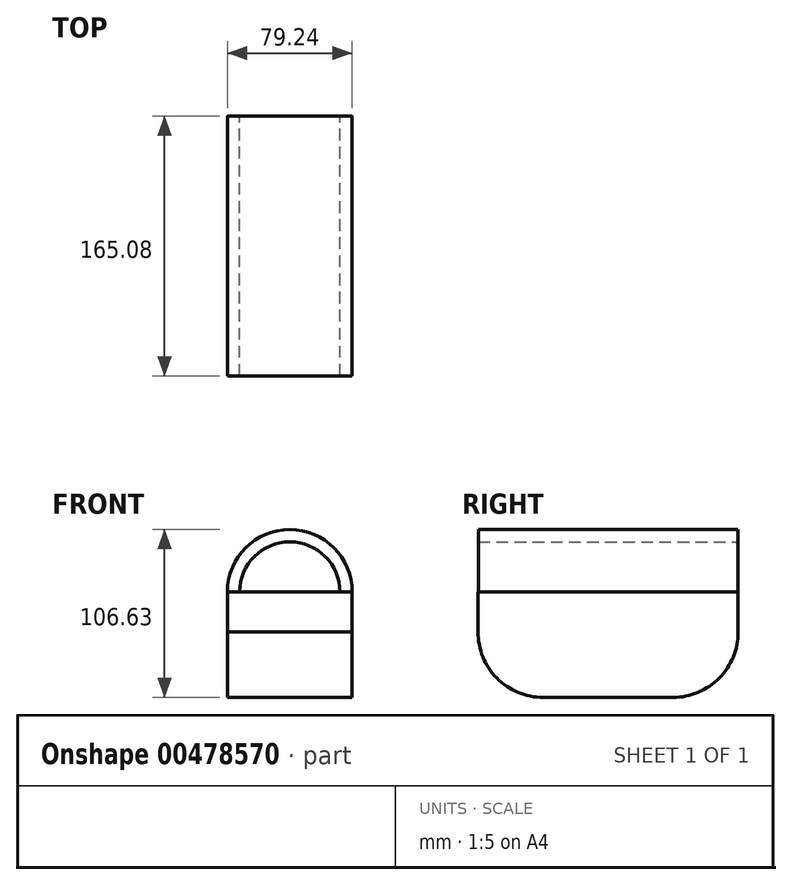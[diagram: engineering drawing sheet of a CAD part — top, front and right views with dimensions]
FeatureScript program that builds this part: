
annotation { "Feature Type Name" : "Feature", "Feature Type Description" : "" }
export const myFeature = defineFeature(function(context is Context, id is Id, definition is map)
    precondition{}
    {
        {
            var Q0;
            Q0=qCreatedBy(makeId("Front.planeOp"),FACE);
            var sketch = newSketch(context, id + "F0", { "sketchPlane" : qUnion([Q0])});
            skPoint(sketch, "E0.end.orphan", {"position": v(-39.32, 0) * mm});
            skPoint(sketch, "E0.start.orphan", {"position": v(39.32, 0) * mm});
            skArc(sketch, "E1", {"start": v(39.62, 0) * mm, "mid": v(0, 39.62) * mm, "end": v(-39.62, 0) * mm});
            skArc(sketch, "E2", {"start": v(31.8, 0) * mm, "mid": v(0, 31.8) * mm, "end": v(-31.8, 0) * mm});
            skLineSegment(sketch, "E3", {"start": v(39.32, 0) * mm, "end": v(39.62, 0) * mm});
            skLineSegment(sketch, "E4", {"start": v(31.8, 0) * mm, "end": v(39.62, 0) * mm});
            skPoint(sketch, "E5.end.orphan", {"position": v(-31.8, -66.6) * mm});
            skPoint(sketch, "E5.start.orphan", {"position": v(-39.62, -66.6) * mm});
            skLineSegment(sketch, "E6", {"start": v(-39.32, 0) * mm, "end": v(-31.8, 0) * mm});
            skLineSegment(sketch, "E7.MirrorCS", {"start": v(-31.8, 0) * mm, "end": v(-39.62, 0) * mm});
            skPoint(sketch, "E8.MirrorCS.start.orphan", {"position": v(-31.8, 0) * mm});
            skPoint(sketch, "E9.MirrorCS.start.orphan", {"position": v(-39.62, 0) * mm});
            skPoint(sketch, "E10.MirrorCS.end.orphan", {"position": v(31.8, -66.6) * mm});
            skPoint(sketch, "E10.MirrorCS.start.orphan", {"position": v(31.8, 0) * mm});
            skPoint(sketch, "E11.MirrorCS.end.orphan", {"position": v(39.62, -66.6) * mm});
            skPoint(sketch, "E11.MirrorCS.start.orphan", {"position": v(39.62, 0) * mm});
            skSolve(sketch);
        }
        {
            var Q0;
            {var subQ1=sQuery(id+"F0.wireOp",EDGE,"E1");Q0=makeQuery(id+"F0.imprint","IMPRINT",FACE,{"disambiguationData":[TD([[makeQuery(id+"F0.imprint","IMPRINT",EDGE,{"derivedFrom":subQ1}),1.0]])]});}
            extrude(context, id + "F1", {"entities" : qUnion([Q0]), "depth" : 82.42 * mm, "hasSecondDirection" : true, "secondDirectionOppositeDirection" : true, "secondDirectionDepth" : 82.42 * mm});
        }
        {
            var Q0;
            Q0=qCreatedBy(makeId("Right.planeOp"),FACE);
            var sketch = newSketch(context, id + "F2", { "sketchPlane" : qUnion([Q0])});
            skLineSegment(sketch, "E12", {"start": v(0, -67.01) * mm, "end": v(-41.35, -67.01) * mm});
            skLineSegment(sketch, "E13", {"start": v(-82.53, 0) * mm, "end": v(-82.53, -25.34) * mm});
            skArc(sketch, "E14", {"start": v(-82.53, -25.34) * mm, "mid": v(-70.65, -54.78) * mm, "end": v(-41.35, -67.01) * mm});
            skArc(sketch, "E15.MirrorCS", {"start": v(82.53, -25.34) * mm, "mid": v(70.65, -54.78) * mm, "end": v(41.35, -67.01) * mm});
            skLineSegment(sketch, "E16.MirrorCS", {"start": v(0, -67.01) * mm, "end": v(41.35, -67.01) * mm});
            skLineSegment(sketch, "E17.MirrorCS", {"start": v(82.53, 0) * mm, "end": v(82.53, -25.34) * mm});
            skLineSegment(sketch, "E18", {"start": v(41.35, -67.01) * mm, "end": v(41.35, -67.01) * mm});
            skLineSegment(sketch, "E19.MirrorCS", {"start": v(-41.35, -67.01) * mm, "end": v(-41.35, -67.01) * mm});
            skLineSegment(sketch, "E20", {"start": v(82.53, 0) * mm, "end": v(-82.53, 0) * mm});
            skPoint(sketch, "E21.MirrorCS.end.orphan", {"position": v(-83.03, -67) * mm});
            skPoint(sketch, "E21.MirrorCS.start.orphan", {"position": v(-82.53, -25.34) * mm});
            skPoint(sketch, "E22.end.orphan", {"position": v(83.03, -67) * mm});
            skSolve(sketch);
        }
        {
            var Q0;
            Q0=makeQuery(id+"F2.imprint","IMPRINT",FACE,{"disambiguationData":[TD([[makeQuery(id+"F2.imprint","IMPRINT",EDGE,{"derivedFrom":sQuery(id+"F2.wireOp",EDGE,"E12")}),-1.0]])]});
            var Q1;
            Q1=sQuery(id+"F2.wireOp",EDGE,"E17.MirrorCS");
            var Q2;
            Q2=sQuery(id+"F2.wireOp",EDGE,"E15.MirrorCS");
            extrude(context, id + "F3", {"entities" : qUnion([Q0]), "surfaceEntities" : qUnion([Q1, Q2]), "endBound" : BoundingType.SYMMETRIC, "depth" : 79.25 * mm, "hasSecondDirection" : true, "secondDirectionOppositeDirection" : true, "secondDirectionDepth" : 39.12 * mm});
        }
    });
